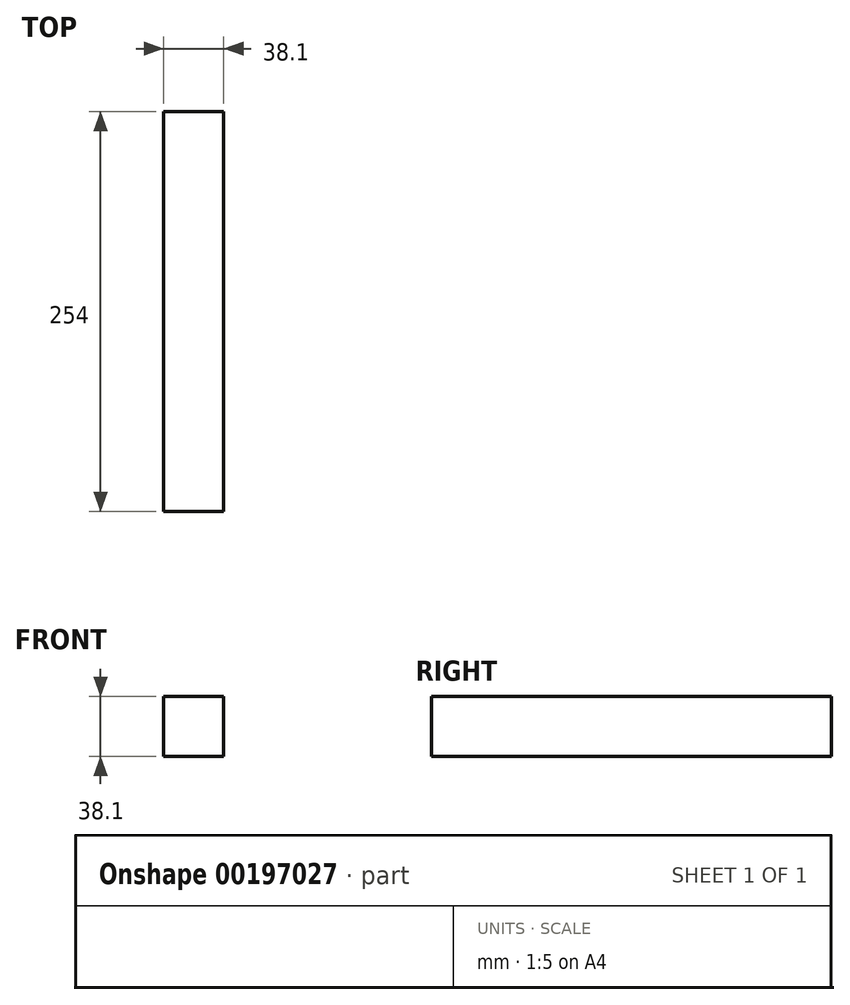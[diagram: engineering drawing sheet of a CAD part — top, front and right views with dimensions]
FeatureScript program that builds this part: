
annotation { "Feature Type Name" : "Feature", "Feature Type Description" : "" }
export const myFeature = defineFeature(function(context is Context, id is Id, definition is map)
    precondition{}
    {
        {
            var Q0;
            Q0=qCreatedBy(makeId("Front.planeOp"),FACE);
            var sketch = newSketch(context, id + "F0", { "sketchPlane" : qUnion([Q0])});
            skLineSegment(sketch, "E0.bottom", {"start": v(0, 0) * mm, "end": v(38.1, 0) * mm});
            skLineSegment(sketch, "E0.top", {"start": v(0, 38.1) * mm, "end": v(38.1, 38.1) * mm});
            skLineSegment(sketch, "E0.left", {"start": v(0, 0) * mm, "end": v(0, 38.1) * mm});
            skLineSegment(sketch, "E0.right", {"start": v(38.1, 0) * mm, "end": v(38.1, 38.1) * mm});
            skSolve(sketch);
        }
        {
            var Q0;
            Q0=makeQuery(id+"F0.imprint","IMPRINT",FACE,{"disambiguationData":[TD([[makeQuery(id+"F0.imprint","IMPRINT",EDGE,{"derivedFrom":sQuery(id+"F0.wireOp",EDGE,"E0.bottom")}),1.0]])]});
            extrude(context, id + "F1", {"entities" : qUnion([Q0]), "depth" : 254 * mm});
        }
    });
